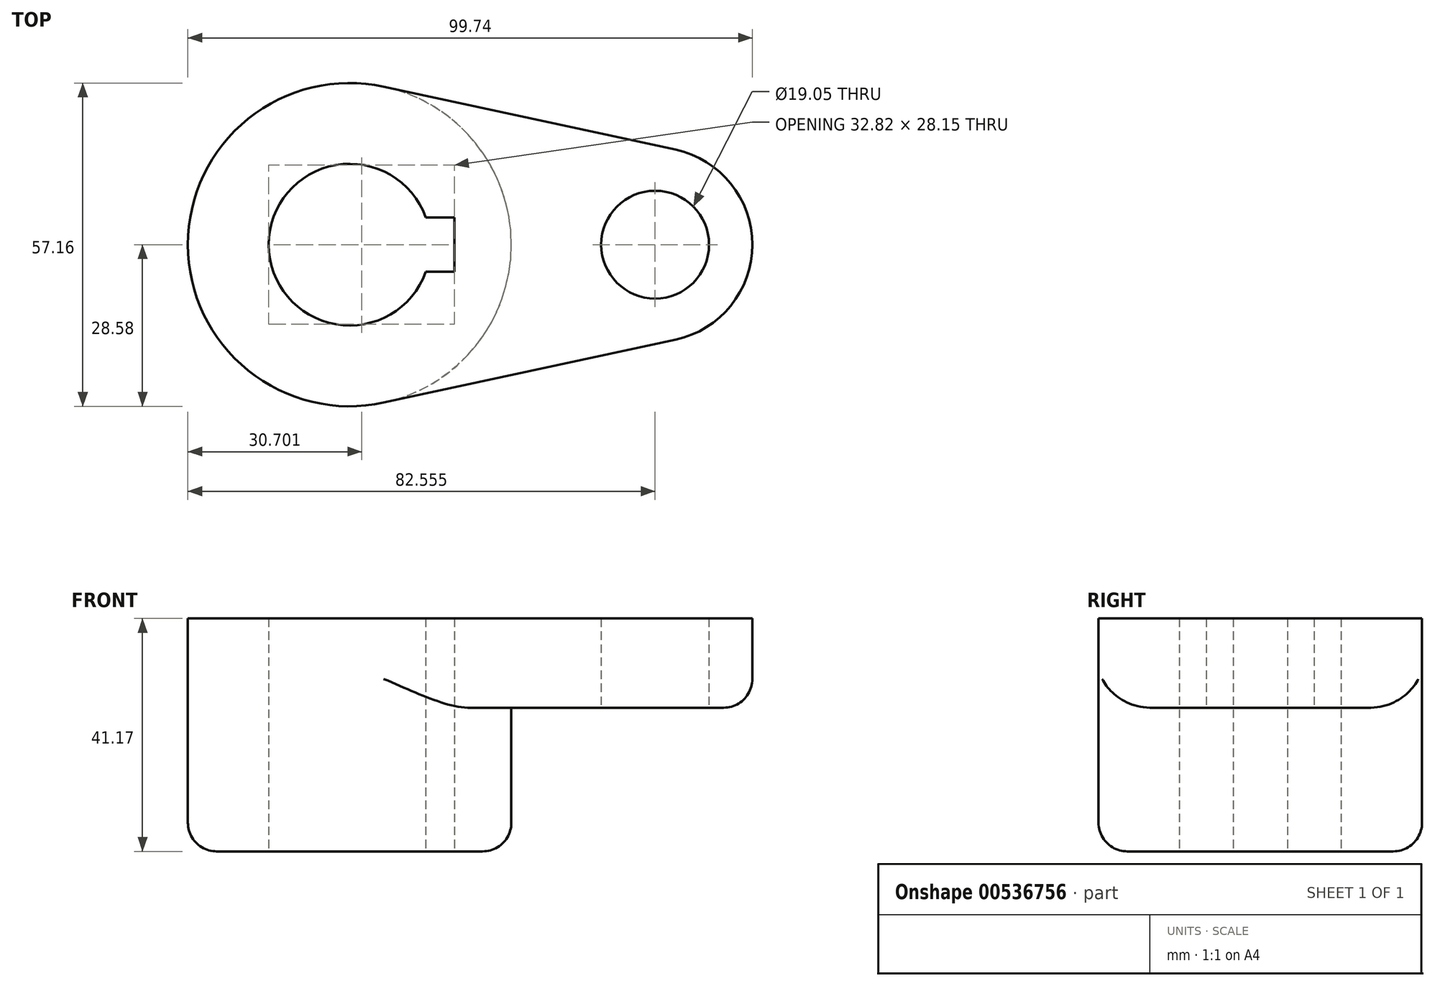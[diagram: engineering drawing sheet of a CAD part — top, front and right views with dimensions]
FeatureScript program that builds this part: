
annotation { "Feature Type Name" : "Feature", "Feature Type Description" : "" }
export const myFeature = defineFeature(function(context is Context, id is Id, definition is map)
    precondition{}
    {
        {
            var Q0;
            Q0=qCreatedBy(makeId("Top.planeOp"),FACE);
            var sketch = newSketch(context, id + "F0", { "sketchPlane" : qUnion([Q0])});
            skCircle(sketch, "E0", {"center": v(0, 0) * mm, "radius": 28.58 * mm});
            skArc(sketch, "E1", {"start": v(57.6, -16.8) * mm, "mid": v(71.16, 0) * mm, "end": v(57.6, 16.8) * mm});
            skLineSegment(sketch, "E2", {"start": v(57.6, 16.8) * mm, "end": v(6.03, 27.93) * mm});
            skLineSegment(sketch, "E3", {"start": v(57.6, -16.8) * mm, "end": v(6.03, -27.93) * mm});
            skCircle(sketch, "E4", {"center": v(53.98, 0) * mm, "radius": 9.53 * mm});
            skPoint(sketch, "E5.centerSnap0", {"position": v(71.16, 0) * mm});
            skArc(sketch, "E6", {"start": v(13.45, 4.81) * mm, "mid": v(-14.29, 0) * mm, "end": v(13.45, -4.81) * mm});
            skLineSegment(sketch, "E7", {"start": v(13.45, 4.81) * mm, "end": v(18.53, 4.81) * mm});
            skLineSegment(sketch, "E8", {"start": v(18.53, 4.81) * mm, "end": v(18.53, -4.81) * mm});
            skLineSegment(sketch, "E9", {"start": v(18.53, -4.81) * mm, "end": v(13.45, -4.81) * mm});
            skSolve(sketch);
        }
        {
            var Q0;
            Q0=makeQuery(id+"F0.imprint","IMPRINT",FACE,{"disambiguationData":[TD([[makeQuery(id+"F0.imprint","IMPRINT",EDGE,{"derivedFrom":sQuery(id+"F0.wireOp",EDGE,"E6")}),-1.0]])]});
            var Q1;
            Q1=makeQuery(id+"F0.imprint","IMPRINT",FACE,{"disambiguationData":[TD([[makeQuery(id+"F0.imprint","IMPRINT",EDGE,{"derivedFrom":sQuery(id+"F0.wireOp",EDGE,"E1")}),1.0]])]});
            extrude(context, id + "F1", {"entities" : qUnion([Q0, Q1]), "depth" : 15.77 * mm, "offsetDistance" : 25.4 * mm});
        }
        {
            var Q0;
            Q0=makeQuery(id+"F1.opExtrude","CAP_FACE",FACE,{"disambiguationData":[OSD([sQuery(id+"F0.wireOp",EDGE,"E0"),sQuery(id+"F0.wireOp",EDGE,"E1"),sQuery(id+"F0.wireOp",EDGE,"E2"),sQuery(id+"F0.wireOp",EDGE,"E3"),sQuery(id+"F0.wireOp",EDGE,"E4"),sQuery(id+"F0.wireOp",EDGE,"E6"),sQuery(id+"F0.wireOp",EDGE,"E7"),sQuery(id+"F0.wireOp",EDGE,"E8"),sQuery(id+"F0.wireOp",EDGE,"E9")])],"isStart":true});
            var sketch = newSketch(context, id + "F2", { "sketchPlane" : qUnion([Q0])});
            skCircle(sketch, "E10", {"center": v(0, 0) * mm, "radius": 28.58 * mm});
            skSolve(sketch);
        }
        {
            var Q0;
            {var subQ0=sQuery(id+"F2.wireOp",EDGE,"E10");Q0=makeQuery(id+"F2.imprint","IMPRINT",FACE,{"disambiguationData":[TD([[makeQuery(id+"F2.imprint","IMPRINT",EDGE,{"disambiguationData":[OD(0.0)],"derivedFrom":subQ0}),-1.0]])]});}
            extrude(context, id + "F3", {"entities" : qUnion([Q0]), "operationType" : NewBodyOperationType.ADD, "depth" : 25.4 * mm, "offsetDistance" : 25.4 * mm});
        }
        {
            var Q0;
            Q0=makeQuery(id+"F3.opExtrude","CAP_EDGE",EDGE,{"disambiguationData":[OSD([sQuery(id+"F2.wireOp",EDGE,"E10")])],"isStart":false});
            fillet(context, id + "F4", {"entities" : qUnion([Q0]), "radius" : 5.08 * mm, "tangentPropagation" : true, "allowEdgeOverflow" : false});
        }
        {
            var Q0;
            Q0=makeQuery(id+"F1.opExtrude","CAP_EDGE",EDGE,{"disambiguationData":[OSD([sQuery(id+"F0.wireOp",EDGE,"E2")])],"isStart":true});
            var Q1;
            Q1=makeQuery(id+"F1.opExtrude","CAP_EDGE",EDGE,{"disambiguationData":[OSD([sQuery(id+"F0.wireOp",EDGE,"E1")])],"isStart":true});
            var Q2;
            Q2=makeQuery(id+"F1.opExtrude","CAP_EDGE",EDGE,{"disambiguationData":[OSD([sQuery(id+"F0.wireOp",EDGE,"E3")])],"isStart":true});
            fillet(context, id + "F5", {"entities" : qUnion([Q0, Q1, Q2]), "radius" : 5.08 * mm, "tangentPropagation" : true, "allowEdgeOverflow" : false});
        }
    });
